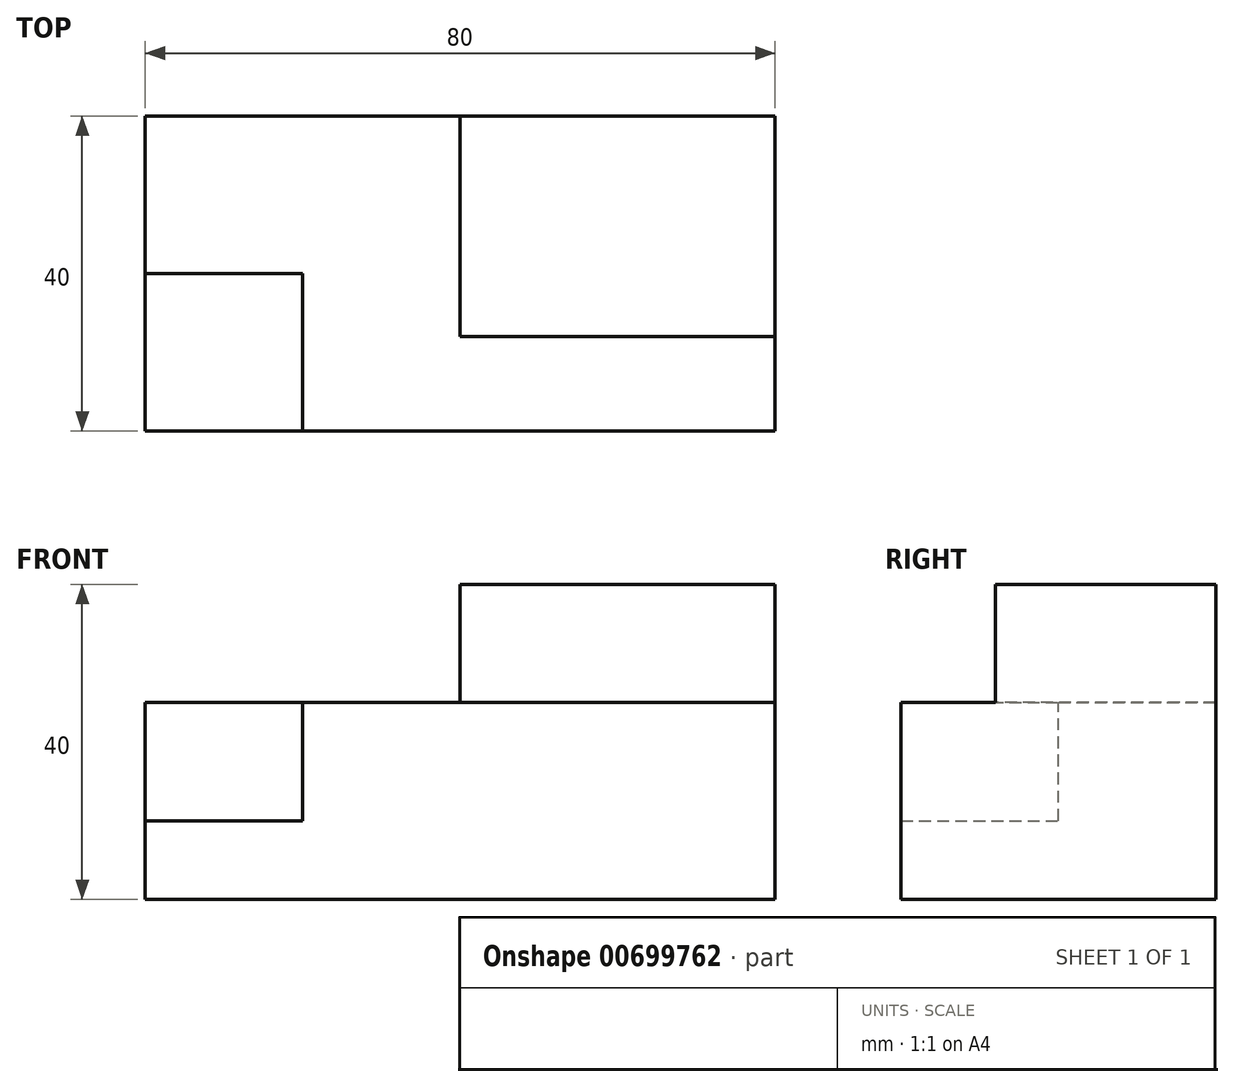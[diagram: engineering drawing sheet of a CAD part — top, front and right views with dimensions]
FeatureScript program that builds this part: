
annotation { "Feature Type Name" : "Feature", "Feature Type Description" : "" }
export const myFeature = defineFeature(function(context is Context, id is Id, definition is map)
    precondition{}
    {
        {
            var Q0;
            Q0=qCreatedBy(makeId("Top.planeOp"),FACE);
            var sketch = newSketch(context, id + "F0", { "sketchPlane" : qUnion([Q0])});
            skLineSegment(sketch, "E0.bottom", {"start": v(40, -20) * mm, "end": v(-40, -20) * mm});
            skLineSegment(sketch, "E0.top", {"start": v(40, 20) * mm, "end": v(-40, 20) * mm});
            skLineSegment(sketch, "E0.left", {"start": v(40, -20) * mm, "end": v(40, 20) * mm});
            skLineSegment(sketch, "E0.right", {"start": v(-40, -20) * mm, "end": v(-40, 20) * mm});
            skPoint(sketch, "E0.middle", {"position": v(0, 0) * mm});
            skSolve(sketch);
        }
        {
            var Q0;
            Q0=makeQuery(id+"F0.imprint","IMPRINT",FACE,{"disambiguationData":[TD([[makeQuery(id+"F0.imprint","IMPRINT",EDGE,{"derivedFrom":sQuery(id+"F0.wireOp",EDGE,"E0.bottom")}),-1.0]])]});
            extrude(context, id + "F1", {"entities" : qUnion([Q0]), "depth" : 25 * mm, "offsetDistance" : 25 * mm});
        }
        {
            var Q0;
            Q0=makeQuery(id+"F1.opExtrude","CAP_FACE",FACE,{"disambiguationData":[OSD([sQuery(id+"F0.wireOp",EDGE,"E0.bottom"),sQuery(id+"F0.wireOp",EDGE,"E0.top"),sQuery(id+"F0.wireOp",EDGE,"E0.left"),sQuery(id+"F0.wireOp",EDGE,"E0.right")])],"isStart":false});
            var sketch = newSketch(context, id + "F2", { "sketchPlane" : qUnion([Q0])});
            skLineSegment(sketch, "E1.bottom", {"start": v(40, 20) * mm, "end": v(0, 20) * mm});
            skLineSegment(sketch, "E1.top", {"start": v(40, -8) * mm, "end": v(0, -8) * mm});
            skLineSegment(sketch, "E1.left", {"start": v(40, 20) * mm, "end": v(40, -8) * mm});
            skLineSegment(sketch, "E1.right", {"start": v(0, 20) * mm, "end": v(0, -8) * mm});
            skSolve(sketch);
        }
        {
            var Q0;
            Q0 = qSketchRegion(id + "F2", true);
            extrude(context, id + "F3", {"entities" : qUnion([Q0]), "operationType" : NewBodyOperationType.ADD, "depth" : 15 * mm, "offsetDistance" : 25 * mm});
        }
        {
            var Q0;
            Q0=makeQuery(id+"F1.opExtrude","CAP_FACE",FACE,{"disambiguationData":[OSD([sQuery(id+"F0.wireOp",EDGE,"E0.bottom"),sQuery(id+"F0.wireOp",EDGE,"E0.top"),sQuery(id+"F0.wireOp",EDGE,"E0.left"),sQuery(id+"F0.wireOp",EDGE,"E0.right")])],"isStart":false});
            var sketch = newSketch(context, id + "F4", { "sketchPlane" : qUnion([Q0])});
            skLineSegment(sketch, "E2.bottom", {"start": v(-40, -20) * mm, "end": v(-20, -20) * mm});
            skLineSegment(sketch, "E2.top", {"start": v(-40, 0) * mm, "end": v(-20, 0) * mm});
            skLineSegment(sketch, "E2.left", {"start": v(-40, -20) * mm, "end": v(-40, 0) * mm});
            skLineSegment(sketch, "E2.right", {"start": v(-20, -20) * mm, "end": v(-20, 0) * mm});
            skSolve(sketch);
        }
        {
            var Q0;
            Q0 = qSketchRegion(id + "F4", true);
            extrude(context, id + "F5", {"entities" : qUnion([Q0]), "operationType" : NewBodyOperationType.REMOVE, "oppositeDirection" : true, "depth" : 15 * mm, "offsetDistance" : 25 * mm});
        }
    });
